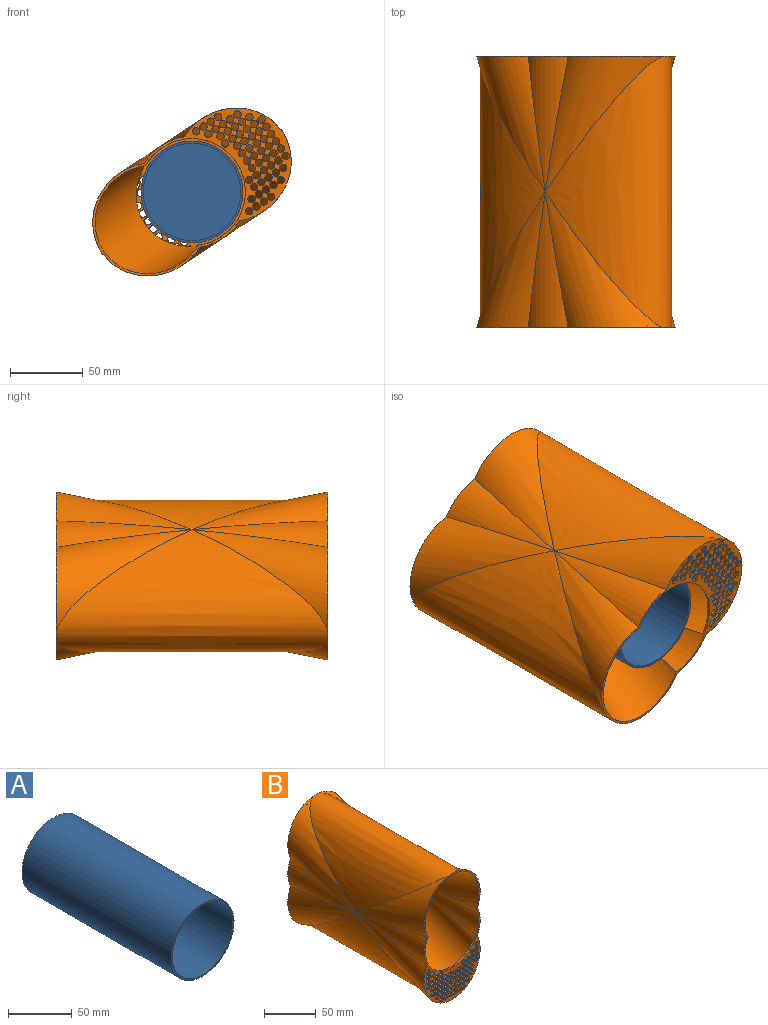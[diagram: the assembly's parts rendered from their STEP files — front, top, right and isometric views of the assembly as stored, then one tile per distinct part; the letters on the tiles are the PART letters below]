
ASSEMBLY  parts=2 mates=1
PART A: 5 faces, bbox 69.9x165.1x69.9 mm
  f0: cylinder r=34.92mm len=165.1mm, axis (0,1,0), area 36229.6mm2, adj f1,f2
  f1: plane 69.85x69.85mm, normal (0,-1,0), area 327.1mm2, adj f0,f3
  f2: plane 69.85x69.85mm, normal (0,1,0), area 3832mm2, adj f0
  f3: cylinder r=33.4mm len=163.58mm, axis (0,1,0), area 34328.8mm2, adj f1,f4
  f4: plane 66.8x66.8mm, normal (0,-1,0), area 3504.8mm2, adj f3
PART B: 185 faces, bbox 114.7x261.3x187.9 mm
  f0: cylinder r=38.1mm len=124.34mm, axis (0,0.94,-0.34), area 3536.8mm2, adj f5,f8,f183
  f1: cylinder r=38.1mm len=124.34mm, axis (0,0.94,0.34), area 3536.8mm2, adj f12,f13,f183
  f2: cylinder r=38.1mm len=124.34mm, axis (0,0.94,-0.34), area 3536.8mm2, adj f11,f13,f182
  f3: cylinder r=38.1mm len=124.34mm, axis (0,0.94,0.34), area 3536.8mm2, adj f5,f7,f182
  f4: cylinder r=36.58mm len=120.95mm, axis (0,0.94,0.34), area 12728.9mm2, adj f15,f21,f22,f80,f82,f84
  f5: plane 187.95x114.74mm, normal (0,-1,0), area 1901.2mm2, adj f0,f3,f6,f7,f8,f9,f15,f16
  f6: cylinder r=38.1mm len=124.34mm, axis (0,0.94,0.34), area 3536.8mm2, adj f5,f8,f182
  f7: cylinder r=38.1mm len=92.83mm, axis (0,1,0), area 1570.6mm2, adj f3,f5,f9
  f8: cylinder r=38.1mm len=92.83mm, axis (0,1,0), area 1570.6mm2, adj f0,f5,f6
  f9: cylinder r=38.1mm len=124.34mm, axis (0,0.94,-0.34), area 3536.8mm2, adj f5,f7,f183
  f10: cylinder r=38.1mm len=124.34mm, axis (0,0.94,0.34), area 3536.8mm2, adj f11,f13,f183
  f11: cylinder r=38.1mm len=92.83mm, axis (0,1,0), area 1570.6mm2, adj f2,f10,f13
  f12: cylinder r=38.1mm len=92.83mm, axis (0,1,0), area 1570.6mm2, adj f1,f13,f14
  f13: plane 155.48x82.27mm, normal (0,1,0), area 7829.8mm2, adj f1,f2,f10,f11,f12,f14,f86,f87
  f14: cylinder r=38.1mm len=124.34mm, axis (0,0.94,-0.34), area 3536.8mm2, adj f12,f13,f182
  f15: cylinder r=36.58mm len=92.83mm, axis (0,1,0), area 3272.7mm2, adj f4,f5,f16,f22
  f16: cylinder r=36.58mm len=105.34mm, axis (0,0.94,-0.34), area 12242.3mm2, adj f5,f15,f17
  f17: cylinder r=36.58mm len=121.83mm, axis (0,0.94,0.34), area 12754.3mm2, adj f16,f18,f19,f20,f113,f114,f123,f124
  f18: cylinder r=36.58mm len=91.31mm, axis (0,1,0), area 1522.2mm2, adj f17,f20,f21
  f19: cylinder r=36.58mm len=91.31mm, axis (0,1,0), area 1522.2mm2, adj f17,f20,f21
  f20: plane 182.66x111.5mm, normal (0,-1,0), area 7165.8mm2, adj f17,f18,f19,f21,f86,f87,f88,f89
  f21: cylinder r=36.58mm len=103.82mm, axis (0,0.94,-0.34), area 12014mm2, adj f4,f18,f19,f20
  f22: plane 75.07x57.97mm, normal (0,1,0), area 1276.1mm2, adj f4,f15,f23,f24,f25,f26,f27,f28
  f23: cylinder r=2.54mm len=5.08mm, axis (0,-1,0), area 24.3mm2, adj f5,f22
  f24: cylinder r=2.54mm len=5.08mm, axis (0,-1,0), area 24.3mm2, adj f5,f22
  f25: cylinder r=2.54mm len=5.08mm, axis (0,-1,0), area 24.3mm2, adj f5,f22
  f26: cylinder r=2.54mm len=5.08mm, axis (0,-1,0), area 24.3mm2, adj f5,f22
  f27: cylinder r=2.54mm len=5.08mm, axis (0,-1,0), area 24.3mm2, adj f5,f22
  f28: cylinder r=2.54mm len=5.08mm, axis (0,-1,0), area 24.3mm2, adj f5,f22
  f29: cylinder r=2.54mm len=5.08mm, axis (0,-1,0), area 24.3mm2, adj f5,f22
  f30: cylinder r=2.54mm len=5.08mm, axis (0,-1,0), area 24.3mm2, adj f5,f22
  f31: cylinder r=2.54mm len=5.08mm, axis (0,-1,0), area 24.3mm2, adj f5,f22
  f32: cylinder r=2.54mm len=5.08mm, axis (0,-1,0), area 24.3mm2, adj f5,f22
  f33: cylinder r=2.54mm len=5.08mm, axis (0,-1,0), area 24.3mm2, adj f5,f22
  f34: cylinder r=2.54mm len=5.08mm, axis (0,-1,0), area 24.3mm2, adj f5,f22
  f35: cylinder r=2.54mm len=5.08mm, axis (0,-1,0), area 24.3mm2, adj f5,f22
  f36: cylinder r=2.54mm len=5.08mm, axis (0,-1,0), area 24.3mm2, adj f5,f22
  f37: cylinder r=2.54mm len=5.08mm, axis (0,-1,0), area 24.3mm2, adj f5,f22
  f38: cylinder r=2.54mm len=5.08mm, axis (0,-1,0), area 24.3mm2, adj f5,f22
  f39: cylinder r=2.54mm len=5.08mm, axis (0,-1,0), area 24.3mm2, adj f5,f22
  f40: cylinder r=2.54mm len=5.08mm, axis (0,-1,0), area 24.3mm2, adj f5,f22
  f41: cylinder r=2.54mm len=5.08mm, axis (0,-1,0), area 24.3mm2, adj f5,f22
  f42: cylinder r=2.54mm len=5.08mm, axis (0,-1,0), area 24.3mm2, adj f5,f22
  f43: cylinder r=2.54mm len=5.08mm, axis (0,-1,0), area 24.3mm2, adj f5,f22
  f44: cylinder r=2.54mm len=5.08mm, axis (0,-1,0), area 24.3mm2, adj f5,f22
  f45: cylinder r=2.54mm len=5.08mm, axis (0,-1,0), area 24.3mm2, adj f5,f22
  f46: cylinder r=2.54mm len=5.08mm, axis (0,-1,0), area 24.3mm2, adj f5,f22
  f47: cylinder r=2.54mm len=5.08mm, axis (0,-1,0), area 24.3mm2, adj f5,f22
  f48: cylinder r=2.54mm len=5.08mm, axis (0,-1,0), area 24.3mm2, adj f5,f22
  f49: cylinder r=2.54mm len=5.08mm, axis (0,-1,0), area 24.3mm2, adj f5,f22
  f50: cylinder r=2.54mm len=5.08mm, axis (0,-1,0), area 24.3mm2, adj f5,f22
  f51: cylinder r=2.54mm len=5.08mm, axis (0,-1,0), area 24.3mm2, adj f5,f22
  f52: cylinder r=2.54mm len=5.08mm, axis (0,-1,0), area 24.3mm2, adj f5,f22
  f53: cylinder r=2.54mm len=5.08mm, axis (0,-1,0), area 24.3mm2, adj f5,f22
  f54: cylinder r=2.54mm len=5.08mm, axis (0,-1,0), area 24.3mm2, adj f5,f22
  f55: cylinder r=2.54mm len=5.08mm, axis (0,-1,0), area 24.3mm2, adj f5,f22
  f56: cylinder r=2.54mm len=5.08mm, axis (0,-1,0), area 24.3mm2, adj f5,f22
  f57: cylinder r=2.54mm len=5.08mm, axis (0,-1,0), area 24.3mm2, adj f5,f22
  f58: cylinder r=2.54mm len=5.08mm, axis (0,-1,0), area 24.3mm2, adj f5,f22
  f59: cylinder r=2.54mm len=5.08mm, axis (0,-1,0), area 24.3mm2, adj f5,f22
  f60: cylinder r=2.54mm len=5.08mm, axis (0,-1,0), area 24.3mm2, adj f5,f22
  f61: cylinder r=2.54mm len=5.08mm, axis (0,-1,0), area 24.3mm2, adj f5,f22
  f62: cylinder r=2.54mm len=5.08mm, axis (0,-1,0), area 24.3mm2, adj f5,f22
  f63: cylinder r=2.54mm len=5.08mm, axis (0,-1,0), area 24.3mm2, adj f5,f22
  f64: cylinder r=2.54mm len=5.08mm, axis (0,-1,0), area 24.3mm2, adj f5,f22
  f65: cylinder r=2.54mm len=5.08mm, axis (0,-1,0), area 24.3mm2, adj f5,f22
  f66: cylinder r=2.54mm len=5.08mm, axis (0,-1,0), area 24.3mm2, adj f5,f22
  f67: cylinder r=2.54mm len=5.08mm, axis (0,-1,0), area 24.3mm2, adj f5,f22
  f68: cylinder r=2.54mm len=5.08mm, axis (0,-1,0), area 24.3mm2, adj f5,f22
  f69: cylinder r=2.54mm len=5.08mm, axis (0,-1,0), area 24.3mm2, adj f5,f22
  f70: cylinder r=2.54mm len=5.08mm, axis (0,-1,0), area 24.3mm2, adj f5,f22
  f71: cylinder r=2.54mm len=5.08mm, axis (0,-1,0), area 24.3mm2, adj f5,f22
  f72: cylinder r=2.54mm len=5.08mm, axis (0,-1,0), area 24.3mm2, adj f5,f22
  f73: cylinder r=2.54mm len=5.08mm, axis (0,-1,0), area 24.3mm2, adj f5,f22
  f74: cylinder r=2.54mm len=5.08mm, axis (0,-1,0), area 24.3mm2, adj f5,f22
  f75: cylinder r=2.54mm len=5.08mm, axis (0,-1,0), area 24.3mm2, adj f5,f22
  f76: cylinder r=2.54mm len=5.08mm, axis (0,-1,0), area 24.3mm2, adj f5,f22
  f77: cylinder r=2.54mm len=5.08mm, axis (0,-1,0), area 24.3mm2, adj f5,f22
  f78: cylinder r=2.54mm len=5.08mm, axis (0,-1,0), area 24.3mm2, adj f5,f22
  f79: cylinder r=2.54mm len=5.08mm, axis (0,-1,0), area 24.3mm2, adj f5,f22
  f80: plane 3.78x2.2mm, normal (0,-1,0), area 3mm2, adj f4,f81
  f81: cylinder r=2.54mm len=5.08mm, axis (0,-1,0), area 24.3mm2, adj f5,f22,f80
  f82: plane 2.4x0.72mm, normal (0,-1,0), area 0.5mm2, adj f4,f83
  f83: cylinder r=2.54mm len=5.08mm, axis (0,-1,0), area 24.3mm2, adj f5,f22,f82
  f84: plane 3.96x2.44mm, normal (0,-1,0), area 3.8mm2, adj f4,f85
  f85: cylinder r=2.54mm len=5.08mm, axis (0,-1,0), area 24.3mm2, adj f5,f22,f84
  f86: cylinder r=2.54mm len=5.08mm, axis (0,1,0), area 24.3mm2, adj f13,f20
  f87: cylinder r=2.54mm len=5.08mm, axis (0,1,0), area 24.3mm2, adj f13,f20
  f88: cylinder r=2.54mm len=5.08mm, axis (0,1,0), area 24.3mm2, adj f13,f20
  f89: cylinder r=2.54mm len=5.08mm, axis (0,1,0), area 24.3mm2, adj f13,f20
  f90: cylinder r=2.54mm len=5.08mm, axis (0,1,0), area 24.3mm2, adj f13,f20
  f91: cylinder r=2.54mm len=5.08mm, axis (0,1,0), area 24.3mm2, adj f13,f20
  f92: cylinder r=2.54mm len=5.08mm, axis (0,1,0), area 24.3mm2, adj f13,f20
  f93: cylinder r=2.54mm len=5.08mm, axis (0,1,0), area 24.3mm2, adj f13,f20
  f94: cylinder r=2.54mm len=5.08mm, axis (0,1,0), area 24.3mm2, adj f13,f20
  f95: cylinder r=2.54mm len=5.08mm, axis (0,1,0), area 24.3mm2, adj f13,f20
  f96: cylinder r=2.54mm len=5.08mm, axis (0,1,0), area 24.3mm2, adj f13,f20
  f97: cylinder r=2.54mm len=5.08mm, axis (0,1,0), area 24.3mm2, adj f13,f20
  f98: cylinder r=2.54mm len=5.08mm, axis (0,1,0), area 24.3mm2, adj f13,f20
  f99: cylinder r=2.54mm len=5.08mm, axis (0,1,0), area 24.3mm2, adj f13,f20
  f100: cylinder r=2.54mm len=5.08mm, axis (0,1,0), area 24.3mm2, adj f13,f20
  f101: cylinder r=2.54mm len=5.08mm, axis (0,1,0), area 24.3mm2, adj f13,f20
  f102: cylinder r=2.54mm len=5.08mm, axis (0,1,0), area 24.3mm2, adj f13,f20
  f103: cylinder r=2.54mm len=5.08mm, axis (0,1,0), area 24.3mm2, adj f13,f20
  f104: cylinder r=2.54mm len=5.08mm, axis (0,1,0), area 24.3mm2, adj f13,f20
  f105: cylinder r=2.54mm len=5.08mm, axis (0,1,0), area 24.3mm2, adj f13,f20
  f106: cylinder r=2.54mm len=5.08mm, axis (0,1,0), area 24.3mm2, adj f13,f20
  f107: cylinder r=2.54mm len=5.08mm, axis (0,1,0), area 24.3mm2, adj f13,f20
  f108: cylinder r=2.54mm len=5.08mm, axis (0,1,0), area 24.3mm2, adj f13,f20
  f109: cylinder r=2.54mm len=5.08mm, axis (0,1,0), area 24.3mm2, adj f13,f20
  f110: cylinder r=2.54mm len=5.08mm, axis (0,1,0), area 24.3mm2, adj f13,f20
  f111: cylinder r=2.54mm len=5.08mm, axis (0,1,0), area 24.3mm2, adj f13,f20
  f112: cylinder r=2.54mm len=5.08mm, axis (0,1,0), area 24.3mm2, adj f13,f20
  f113: plane 3.28x1.59mm, normal (0,1,0), area 1.7mm2, adj f17,f114
  f114: cylinder r=2.54mm len=5.08mm, axis (0,1,0), area 25.3mm2, adj f13,f17,f20,f113
  f115: cylinder r=2.54mm len=5.08mm, axis (0,1,0), area 24.3mm2, adj f13,f20
  f116: cylinder r=2.54mm len=5.08mm, axis (0,1,0), area 24.3mm2, adj f13,f20
  f117: cylinder r=2.54mm len=5.08mm, axis (0,1,0), area 24.3mm2, adj f13,f20
  f118: cylinder r=2.54mm len=5.08mm, axis (0,1,0), area 24.3mm2, adj f13,f20
  f119: cylinder r=2.54mm len=5.08mm, axis (0,1,0), area 24.3mm2, adj f13,f20
  f120: cylinder r=2.54mm len=5.08mm, axis (0,1,0), area 24.3mm2, adj f13,f20
  f121: cylinder r=2.54mm len=5.08mm, axis (0,1,0), area 24.3mm2, adj f13,f20
  f122: cylinder r=2.54mm len=5.08mm, axis (0,1,0), area 24.3mm2, adj f13,f20
  f123: plane 3.53x1.77mm, normal (0,1,0), area 2.1mm2, adj f17,f124
  f124: cylinder r=2.54mm len=5.08mm, axis (0,1,0), area 25.4mm2, adj f13,f17,f20,f123
  f125: cylinder r=2.54mm len=5.08mm, axis (0,1,0), area 24.3mm2, adj f13,f20
  f126: cylinder r=2.54mm len=5.08mm, axis (0,1,0), area 24.3mm2, adj f13,f20
  f127: cylinder r=2.54mm len=5.08mm, axis (0,1,0), area 24.3mm2, adj f13,f20
  f128: cylinder r=2.54mm len=5.08mm, axis (0,1,0), area 24.3mm2, adj f13,f20
  f129: cylinder r=2.54mm len=5.08mm, axis (0,1,0), area 24.3mm2, adj f13,f20
  f130: cylinder r=2.54mm len=5.08mm, axis (0,1,0), area 24.3mm2, adj f13,f20
  f131: cylinder r=2.54mm len=5.08mm, axis (0,1,0), area 24.3mm2, adj f13,f20
  f132: cylinder r=2.54mm len=5.08mm, axis (0,1,0), area 24.3mm2, adj f13,f20
  f133: cylinder r=2.54mm len=5.08mm, axis (0,1,0), area 24.3mm2, adj f13,f20
  f134: cylinder r=2.54mm len=5.08mm, axis (0,1,0), area 24.3mm2, adj f13,f20
  f135: cylinder r=2.54mm len=5.08mm, axis (0,1,0), area 24.3mm2, adj f13,f20
  f136: cylinder r=2.54mm len=5.08mm, axis (0,1,0), area 24.3mm2, adj f13,f20
  f137: cylinder r=2.54mm len=5.08mm, axis (0,1,0), area 24.3mm2, adj f13,f20
  f138: cylinder r=2.54mm len=5.08mm, axis (0,1,0), area 24.3mm2, adj f13,f20
  f139: cylinder r=2.54mm len=5.08mm, axis (0,1,0), area 24.3mm2, adj f13,f20
  f140: cylinder r=2.54mm len=5.08mm, axis (0,1,0), area 24.3mm2, adj f13,f20
  f141: cylinder r=2.54mm len=5.08mm, axis (0,1,0), area 24.3mm2, adj f13,f20
  f142: cylinder r=2.54mm len=5.08mm, axis (0,1,0), area 24.3mm2, adj f13,f20
  f143: cylinder r=2.54mm len=5.08mm, axis (0,1,0), area 24.3mm2, adj f13,f20
  f144: cylinder r=2.54mm len=5.08mm, axis (0,1,0), area 24.3mm2, adj f13,f20
  f145: cylinder r=2.54mm len=5.08mm, axis (0,1,0), area 24.3mm2, adj f13,f20
  f146: cylinder r=2.54mm len=5.08mm, axis (0,1,0), area 24.3mm2, adj f13,f20
  f147: cylinder r=2.54mm len=5.08mm, axis (0,1,0), area 24.3mm2, adj f13,f20
  f148: cylinder r=2.54mm len=5.08mm, axis (0,1,0), area 24.3mm2, adj f13,f20
  f149: cylinder r=2.54mm len=5.08mm, axis (0,1,0), area 24.3mm2, adj f13,f20
  f150: cylinder r=2.54mm len=5.08mm, axis (0,1,0), area 24.3mm2, adj f13,f20
  f151: cylinder r=2.54mm len=5.08mm, axis (0,1,0), area 24.3mm2, adj f13,f20
  f152: cylinder r=2.54mm len=5.08mm, axis (0,1,0), area 24.3mm2, adj f13,f20
  f153: cylinder r=2.54mm len=5.08mm, axis (0,1,0), area 24.3mm2, adj f13,f20
  f154: cylinder r=2.54mm len=5.08mm, axis (0,1,0), area 24.3mm2, adj f13,f20
  f155: cylinder r=2.54mm len=5.08mm, axis (0,1,0), area 24.3mm2, adj f13,f20
  f156: cylinder r=2.54mm len=5.08mm, axis (0,1,0), area 24.3mm2, adj f13,f20
  f157: cylinder r=2.54mm len=5.08mm, axis (0,1,0), area 24.3mm2, adj f13,f20
  f158: cylinder r=2.54mm len=5.08mm, axis (0,1,0), area 24.3mm2, adj f13,f20
  f159: cylinder r=2.54mm len=5.08mm, axis (0,1,0), area 24.3mm2, adj f13,f20
  f160: cylinder r=2.54mm len=5.08mm, axis (0,1,0), area 24.3mm2, adj f13,f20
  f161: cylinder r=2.54mm len=5.08mm, axis (0,1,0), area 24.3mm2, adj f13,f20
  f162: cylinder r=2.54mm len=5.08mm, axis (0,1,0), area 24.3mm2, adj f13,f20
  f163: cylinder r=2.54mm len=5.08mm, axis (0,1,0), area 24.3mm2, adj f13,f20
  f164: plane 3.25x1.52mm, normal (0,1,0), area 1.6mm2, adj f17,f165
  f165: cylinder r=2.54mm len=5.08mm, axis (0,1,0), area 25.3mm2, adj f13,f17,f20,f164
  f166: cylinder r=2.54mm len=5.08mm, axis (0,1,0), area 24.3mm2, adj f13,f20
  f167: cylinder r=2.54mm len=5.08mm, axis (0,1,0), area 24.3mm2, adj f13,f20
  f168: cylinder r=2.54mm len=5.08mm, axis (0,1,0), area 24.3mm2, adj f13,f20
  f169: cylinder r=2.54mm len=5.08mm, axis (0,1,0), area 24.3mm2, adj f13,f20
  f170: cylinder r=2.54mm len=5.08mm, axis (0,1,0), area 24.3mm2, adj f13,f20
  f171: cylinder r=2.54mm len=5.08mm, axis (0,1,0), area 24.3mm2, adj f13,f20
  f172: cylinder r=2.54mm len=5.08mm, axis (0,1,0), area 24.3mm2, adj f13,f20
  f173: cylinder r=2.54mm len=5.08mm, axis (0,1,0), area 24.3mm2, adj f13,f20
  f174: cylinder r=2.54mm len=5.08mm, axis (0,1,0), area 24.3mm2, adj f13,f20
  f175: cylinder r=2.54mm len=5.08mm, axis (0,1,0), area 24.3mm2, adj f13,f20
  f176: cylinder r=2.54mm len=5.08mm, axis (0,1,0), area 24.3mm2, adj f13,f20
  f177: cylinder r=2.54mm len=5.08mm, axis (0,1,0), area 24.3mm2, adj f13,f20
  f178: cylinder r=2.54mm len=5.08mm, axis (0,1,0), area 24.3mm2, adj f13,f20
  f179: cylinder r=2.54mm len=5.08mm, axis (0,1,0), area 24.3mm2, adj f13,f20
  f180: cylinder r=2.54mm len=5.08mm, axis (0,1,0), area 24.3mm2, adj f13,f20
  f181: cylinder r=2.54mm len=5.08mm, axis (0,1,0), area 24.3mm2, adj f13,f20
  f182: bspline ~186.78x76.21mm, area 19386.7mm2, adj f2,f3,f5,f6,f13,f14
  f183: bspline ~186.78x76.21mm, area 19386.7mm2, adj f0,f1,f5,f9,f10,f13
  f184: cylinder r=6.35mm len=12.7mm, axis (0,1,0), area 60.8mm2, adj f13,f20
PLACE A t=(0,-4.06,0)mm fixed
PLACE B rot(axis=(0,-1,0),123.5deg) t=(0,0,0)mm
MATE revolute A.f0 <-> B.f7  axis (0,1,0) through (0,-4.06,0)mm
